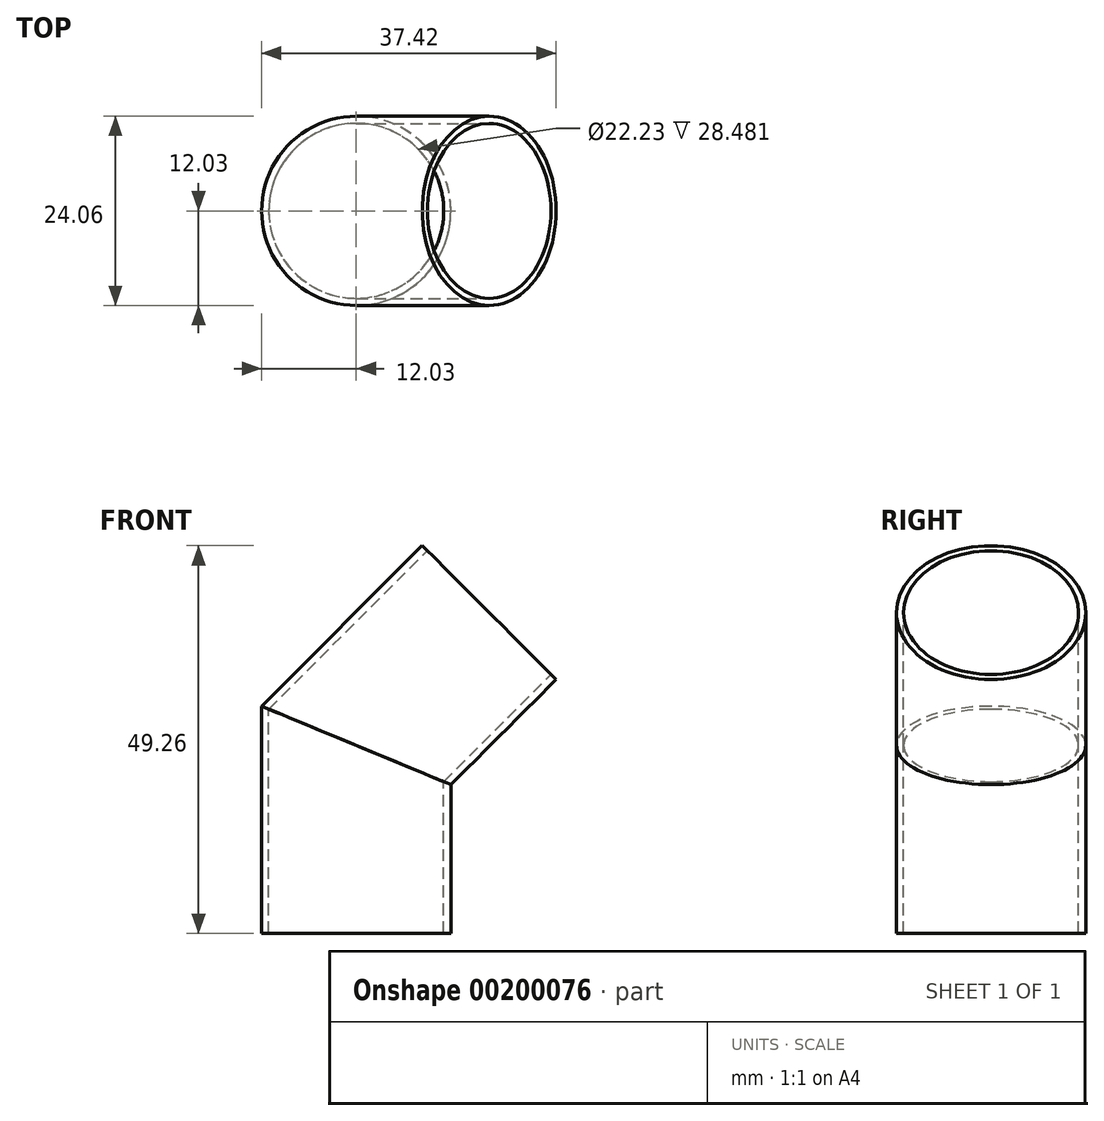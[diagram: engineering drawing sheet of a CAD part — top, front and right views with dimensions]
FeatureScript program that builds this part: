
annotation { "Feature Type Name" : "Feature", "Feature Type Description" : "" }
export const myFeature = defineFeature(function(context is Context, id is Id, definition is map)
    precondition{}
    {
        {
            var Q0;
            Q0=qCreatedBy(makeId("Top.planeOp"),FACE);
            var sketch = newSketch(context, id + "F0", { "sketchPlane" : qUnion([Q0])});
            skCircle(sketch, "E0", {"center": v(0, 0) * mm, "radius": 12.03 * mm});
            skCircle(sketch, "E1", {"center": v(0, 0) * mm, "radius": 11.11 * mm});
            skSolve(sketch);
        }
        {
            var Q0;
            Q0=qCreatedBy(makeId("Front.planeOp"),FACE);
            var sketch = newSketch(context, id + "F1", { "sketchPlane" : qUnion([Q0])});
            skLineSegment(sketch, "E2", {"start": v(0, 0) * mm, "end": v(0, 23.88) * mm});
            skLineSegment(sketch, "E3", {"start": v(16.88, 40.76) * mm, "end": v(0, 23.88) * mm});
            skLineSegment(sketch, "E4.0", {"start": v(-12.07, 0) * mm, "end": v(-12.07, 28.87) * mm});
            skLineSegment(sketch, "E4.1", {"start": v(8.35, 49.3) * mm, "end": v(-12.07, 28.87) * mm});
            skSolve(sketch);
        }
        {
            var Q0;
            Q0=makeQuery(id+"F0.imprint","IMPRINT",FACE,{"disambiguationData":[TD([[makeQuery(id+"F0.imprint","IMPRINT",EDGE,{"derivedFrom":sQuery(id+"F0.wireOp",EDGE,"E0")}),1.0]])]});
            var Q1;
            Q1=sQuery(id+"F1.wireOp",EDGE,"E4.0");
            var Q2;
            Q2=sQuery(id+"F1.wireOp",EDGE,"E4.1");
            sweep(context, id + "F2", {"profiles" : qUnion([Q0]), "path" : qUnion([Q1, Q2])});
        }
    });
